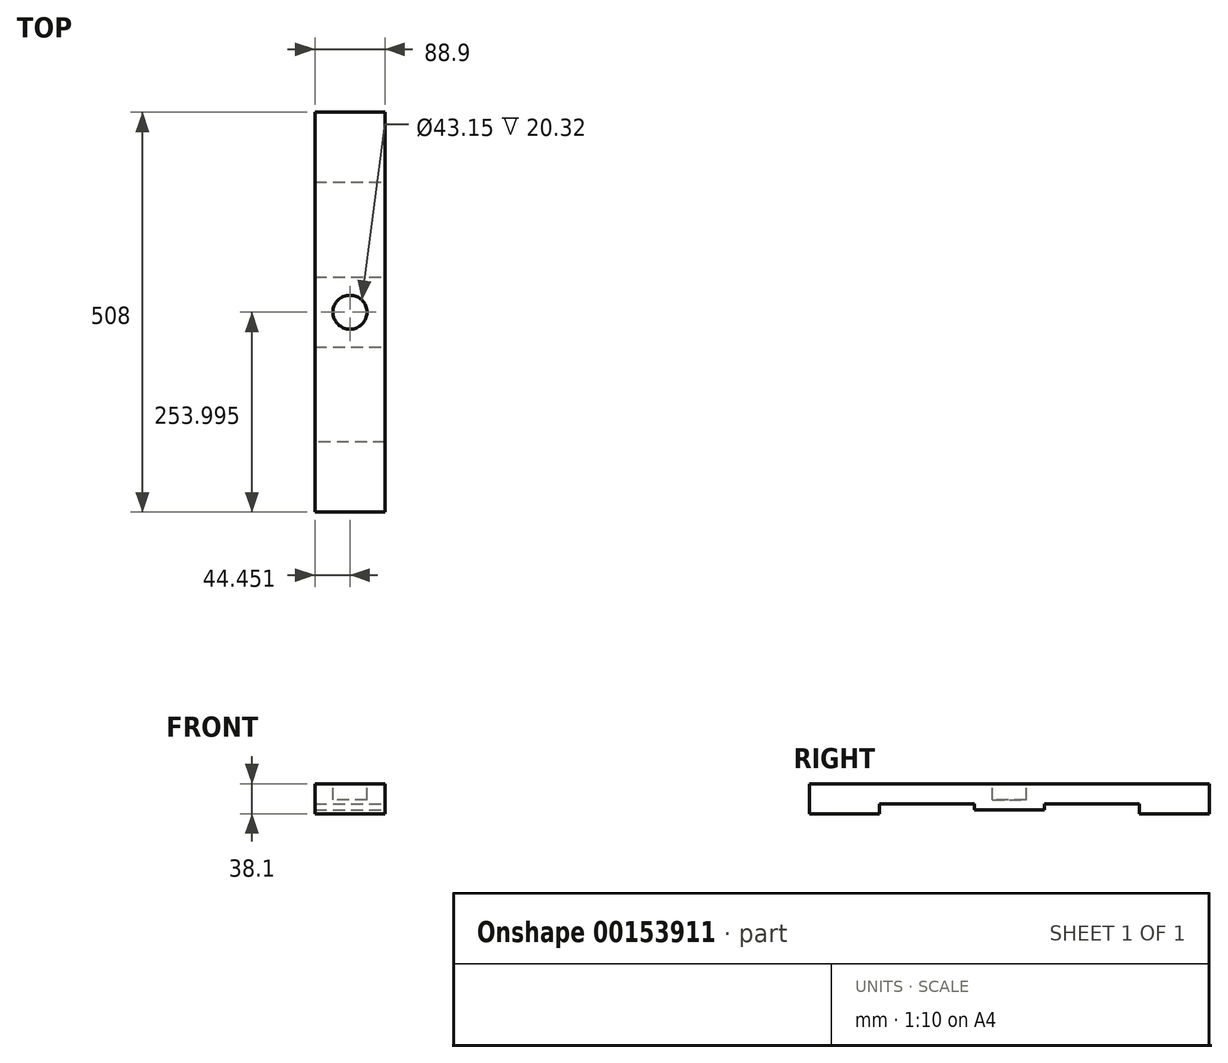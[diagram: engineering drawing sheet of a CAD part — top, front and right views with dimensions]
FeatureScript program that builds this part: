
annotation { "Feature Type Name" : "Feature", "Feature Type Description" : "" }
export const myFeature = defineFeature(function(context is Context, id is Id, definition is map)
    precondition{}
    {
        {
            var Q0;
            Q0=qCreatedBy(makeId("Front.planeOp"),FACE);
            var sketch = newSketch(context, id + "F0", { "sketchPlane" : qUnion([Q0])});
            skLineSegment(sketch, "E0.bottom", {"start": v(-49.04, 4.11) * mm, "end": v(39.86, 4.11) * mm});
            skLineSegment(sketch, "E0.top", {"start": v(-49.04, -21.29) * mm, "end": v(39.86, -21.29) * mm});
            skLineSegment(sketch, "E0.left", {"start": v(-49.04, 4.11) * mm, "end": v(-49.04, -21.29) * mm});
            skLineSegment(sketch, "E0.right", {"start": v(39.86, 4.11) * mm, "end": v(39.86, -21.29) * mm});
            skSolve(sketch);
        }
        {
            var Q0;
            Q0 = qSketchRegion(id + "F0", true);
            extrude(context, id + "F1", {"entities" : qUnion([Q0]), "depth" : 508 * mm});
        }
        {
            var Q0;
            Q0=makeQuery(id+"F1.opExtrude","SWEPT_FACE",FACE,{"disambiguationData":[OSD([sQuery(id+"F0.wireOp",EDGE,"E0.top")])]});
            var sketch = newSketch(context, id + "F2", { "sketchPlane" : qUnion([Q0])});
            skLineSegment(sketch, "E1.bottom", {"start": v(-49.04, 88.9) * mm, "end": v(39.86, 88.9) * mm});
            skLineSegment(sketch, "E1.top", {"start": v(-49.04, 0) * mm, "end": v(39.86, 0) * mm});
            skLineSegment(sketch, "E1.left", {"start": v(-49.04, 88.9) * mm, "end": v(-49.04, 0) * mm});
            skLineSegment(sketch, "E1.right", {"start": v(39.86, 88.9) * mm, "end": v(39.86, 0) * mm});
            skLineSegment(sketch, "E2.bottom", {"start": v(39.86, 419.1) * mm, "end": v(-49.04, 419.1) * mm});
            skLineSegment(sketch, "E2.top", {"start": v(39.86, 508) * mm, "end": v(-49.04, 508) * mm});
            skLineSegment(sketch, "E2.left", {"start": v(39.86, 419.1) * mm, "end": v(39.86, 508) * mm});
            skLineSegment(sketch, "E2.right", {"start": v(-49.04, 419.1) * mm, "end": v(-49.04, 508) * mm});
            skPoint(sketch, "E3.startSnap0", {"position": v(-4.6, 88.9) * mm});
            skPoint(sketch, "E3.endSnap0", {"position": v(-4.6, 419.1) * mm});
            skLineSegment(sketch, "E4", {"start": v(-4.6, 88.9) * mm, "end": v(-4.6, 419.1) * mm});
            skLineSegment(sketch, "E5.bottom", {"start": v(-49.04, 254) * mm, "end": v(39.86, 254) * mm});
            skLineSegment(sketch, "E5.top", {"start": v(-49.04, 298.45) * mm, "end": v(39.86, 298.45) * mm});
            skLineSegment(sketch, "E5.left", {"start": v(-49.04, 254) * mm, "end": v(-49.04, 298.45) * mm});
            skLineSegment(sketch, "E5.right", {"start": v(39.86, 254) * mm, "end": v(39.86, 298.45) * mm});
            skLineSegment(sketch, "E6.top", {"start": v(-49.04, 209.55) * mm, "end": v(39.86, 209.55) * mm});
            skLineSegment(sketch, "E6.left", {"start": v(-49.04, 254) * mm, "end": v(-49.04, 209.55) * mm});
            skLineSegment(sketch, "E6.right", {"start": v(39.86, 254) * mm, "end": v(39.86, 209.55) * mm});
            skLineSegment(sketch, "E7.bottom", {"start": v(-49.04, 209.55) * mm, "end": v(-4.6, 209.55) * mm});
            skLineSegment(sketch, "E7.top", {"start": v(-49.04, 298.45) * mm, "end": v(-4.6, 298.45) * mm});
            skLineSegment(sketch, "E7.left", {"start": v(-49.04, 209.55) * mm, "end": v(-49.04, 298.45) * mm});
            skLineSegment(sketch, "E7.right", {"start": v(-4.6, 209.55) * mm, "end": v(-4.6, 298.45) * mm});
            skLineSegment(sketch, "E8", {"start": v(-49.04, 209.55) * mm, "end": v(-4.6, 209.55) * mm, "construction": true});
            skLineSegment(sketch, "E9", {"start": v(-49.04, 298.45) * mm, "end": v(-4.6, 298.45) * mm, "construction": true});
            skLineSegment(sketch, "E10", {"start": v(-4.6, 209.55) * mm, "end": v(39.86, 209.55) * mm, "construction": true});
            skLineSegment(sketch, "E11", {"start": v(-4.6, 298.45) * mm, "end": v(39.86, 298.45) * mm, "construction": true});
            skSolve(sketch);
        }
        {
            var Q0;
            Q0=makeQuery(id+"F2.imprint","IMPRINT",FACE,{"disambiguationData":[TD([[makeQuery(id+"F2.imprint","IMPRINT",EDGE,{"derivedFrom":sQuery(id+"F2.wireOp",EDGE,"E1.top")}),1.0]])]});
            var Q1;
            Q1=makeQuery(id+"F2.imprint","IMPRINT",FACE,{"disambiguationData":[TD([[makeQuery(id+"F2.imprint","IMPRINT",EDGE,{"derivedFrom":sQuery(id+"F2.wireOp",EDGE,"E2.top")}),-1.0]])]});
            extrude(context, id + "F3", {"entities" : qUnion([Q0, Q1]), "operationType" : NewBodyOperationType.ADD, "depth" : 12.7 * mm});
        }
        {
            var Q0;
            Q0=makeQuery(id+"F1.opExtrude","SWEPT_FACE",FACE,{"disambiguationData":[OSD([sQuery(id+"F0.wireOp",EDGE,"E0.top")])]});
            var sketch = newSketch(context, id + "F4", { "sketchPlane" : qUnion([Q0])});
            skLineSegment(sketch, "E12", {"start": v(-4.6, 88.9) * mm, "end": v(-4.6, 419.1) * mm, "construction": true});
            skLineSegment(sketch, "E13", {"start": v(-49.04, 254) * mm, "end": v(39.86, 254) * mm, "construction": true});
            skLineSegment(sketch, "E14.bottom", {"start": v(-49.04, 254) * mm, "end": v(-4.6, 254) * mm, "construction": true});
            skLineSegment(sketch, "E14.top", {"start": v(-49.04, 298.45) * mm, "end": v(-4.6, 298.45) * mm, "construction": true});
            skLineSegment(sketch, "E14.left", {"start": v(-49.04, 254) * mm, "end": v(-49.04, 298.45) * mm, "construction": true});
            skLineSegment(sketch, "E14.right", {"start": v(-4.6, 254) * mm, "end": v(-4.6, 298.45) * mm, "construction": true});
            skLineSegment(sketch, "E15.top", {"start": v(-49.04, 209.55) * mm, "end": v(-4.6, 209.55) * mm, "construction": true});
            skLineSegment(sketch, "E15.left", {"start": v(-49.04, 254) * mm, "end": v(-49.04, 209.55) * mm, "construction": true});
            skLineSegment(sketch, "E15.right", {"start": v(-4.6, 254) * mm, "end": v(-4.6, 209.55) * mm, "construction": true});
            skLineSegment(sketch, "E16.bottom", {"start": v(-4.6, 209.55) * mm, "end": v(39.86, 209.55) * mm});
            skLineSegment(sketch, "E16.top", {"start": v(-4.6, 254) * mm, "end": v(39.86, 254) * mm});
            skLineSegment(sketch, "E16.left", {"start": v(-4.6, 209.55) * mm, "end": v(-4.6, 254) * mm});
            skLineSegment(sketch, "E16.right", {"start": v(39.86, 209.55) * mm, "end": v(39.86, 254) * mm});
            skLineSegment(sketch, "E17.bottom", {"start": v(-4.6, 298.45) * mm, "end": v(39.86, 298.45) * mm});
            skLineSegment(sketch, "E17.left", {"start": v(-4.6, 298.45) * mm, "end": v(-4.6, 254) * mm});
            skLineSegment(sketch, "E17.right", {"start": v(39.86, 298.45) * mm, "end": v(39.86, 254) * mm});
            skLineSegment(sketch, "E18.bottom", {"start": v(-49.04, 209.55) * mm, "end": v(-4.6, 209.55) * mm});
            skLineSegment(sketch, "E18.top", {"start": v(-49.04, 298.45) * mm, "end": v(-4.6, 298.45) * mm});
            skLineSegment(sketch, "E18.left", {"start": v(-49.04, 209.55) * mm, "end": v(-49.04, 298.45) * mm});
            skLineSegment(sketch, "E18.right", {"start": v(-4.6, 209.55) * mm, "end": v(-4.6, 298.45) * mm});
            skSolve(sketch);
        }
        {
            var Q0;
            Q0 = qSketchRegion(id + "F4", true);
            extrude(context, id + "F5", {"entities" : qUnion([Q0]), "operationType" : NewBodyOperationType.ADD, "depth" : 4.44 * mm});
        }
        {
            var Q0;
            Q0 = qSketchRegion(id + "F4", true);
            extrude(context, id + "F6", {"entities" : qUnion([Q0]), "operationType" : NewBodyOperationType.ADD, "depth" : 7.62 * mm});
        }
        {
            var Q0;
            Q0=makeQuery(id+"F1.opExtrude","SWEPT_FACE",FACE,{"disambiguationData":[OSD([sQuery(id+"F0.wireOp",EDGE,"E0.bottom")])]});
            var sketch = newSketch(context, id + "F7", { "sketchPlane" : qUnion([Q0])});
            skLineSegment(sketch, "E19", {"start": v(-4.6, 0) * mm, "end": v(-4.6, -508) * mm, "construction": true});
            skCircle(sketch, "E20", {"center": v(-4.6, -254) * mm, "radius": 21.12 * mm, "construction": true});
            skSolve(sketch);
        }
        {
            var Q0;
            {var subQ0=sQuery(id+"F0.wireOp",EDGE,"E0.bottom");Q0=makeQuery(id+"F7.imprint","IMPRINT",FACE,{"disambiguationData":[TD([[makeQuery(id+"F7.imprint","IMPRINT",EDGE,{"derivedFrom":makeQuery(id+"F1.opExtrude","CAP_EDGE",EDGE,{"disambiguationData":[OSD([subQ0])],"isStart":true})}),-1.0]])]});}
            var sketch = newSketch(context, id + "F8", { "sketchPlane" : qUnion([Q0])});
            skCircle(sketch, "E21", {"center": v(-4.59, -254) * mm, "radius": 21.58 * mm});
            skSolve(sketch);
        }
        {
            var Q0;
            Q0 = qSketchRegion(id + "F8", true);
            extrude(context, id + "F9", {"entities" : qUnion([Q0]), "operationType" : NewBodyOperationType.REMOVE, "oppositeDirection" : true, "depth" : 20.32 * mm});
        }
    });
